# Revit family: Seat-Hussey-Fusion-Aisle_End_Seat
name_source: partatom
category: Specialty Equipment
units: mm (PartAtom-declared; Revit-internal decimal feet)

## family parameters
Always vertical = Yes
Cut with Voids When Loaded = No
Enable Cutting in Views = No
Maintain Annotation Orientation = No
Part Type = Normal
Room Calculation Point = No
Round Connector Dimension = Use Diameter
Shared = No
Work Plane-Based = No

## types (5) — shared parameters
Aisle Stanchion Type = Stanchion-Fusion-Aisle : Floor Mounted
BIM Version = v3.2
CSI MasterFormat = 12 63 00
Default Elevation = 0"
Intermediate Stanchion Type = Stanchion-Fusion : Floor Mounted
Manufacturer = Hussey Seating Company
Model = Fusion
Product Page URL = http://www.husseyseating.com
Seat Back Color = Hussey - 301 Blue
Seat Color = Hussey - 301 Blue
Seat Depth = 1' - 10"
Seat Depth Closed = 1' - 2"
Stanchion Color = Hussey - 301 Blue
Type Comments = Stadium Seating - Aisle
URL = http://www.husseyseating.com

## per-type parameters (varying)
| type | Description | Seat Width |
| 21" | Fusion Fixed Stadium Seat | 1' - 9" |
| 22" |  | 1' - 10" |
| 18" |  | 1' - 6" |
| 19" |  | 1' - 7" |
| 20" |  | 1' - 8" |

## geometry (parser evidence)
native form markers: Sweep x18
no freeform markers — native parametric forms only
